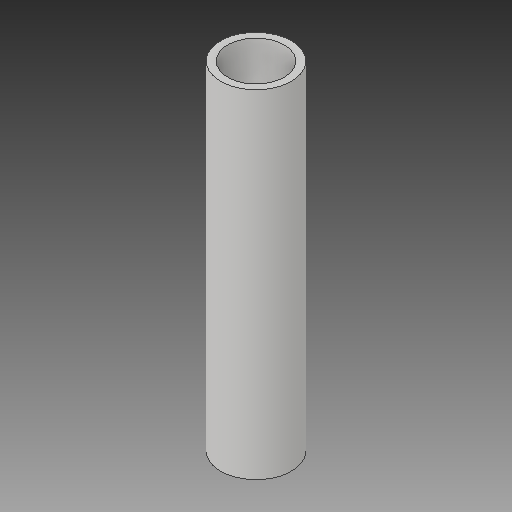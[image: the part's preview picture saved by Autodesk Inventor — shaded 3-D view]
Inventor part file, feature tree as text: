
AUTODESK INVENTOR PART (.ipt)
format: ipt  version: 2019.2 (Build 232265000, 265)  size: 102,400 bytes
history: native  units: mm
features: other x4, plane x1, extrude x1, sketch x1, reference x1
ambient origin geometry x8: Origin, YZ Plane, XZ Plane, XY Plane, X Axis, Y Axis, Z Axis, Center Point
bodies: Body1 (feature_tree)
feature tree (8):
  plane  "Work Plane2"
  extrude  "Extrusion2"  Depth=76.0mm
  sketch  "Sketch2"  dims[d4=15.875mm d5=1.6mm d6=76.0mm d7=0.0mm]
  reference  "Reference2"
  other  "<userpath>\Desktop\3dprojects\OpenEmoto\Hub\Hub.iam"
  other  "Hub.iam"
  other  "Bearing:2"
  other  "DIN 628 SKF - 7..B SKF 7200 BECBP:1"
